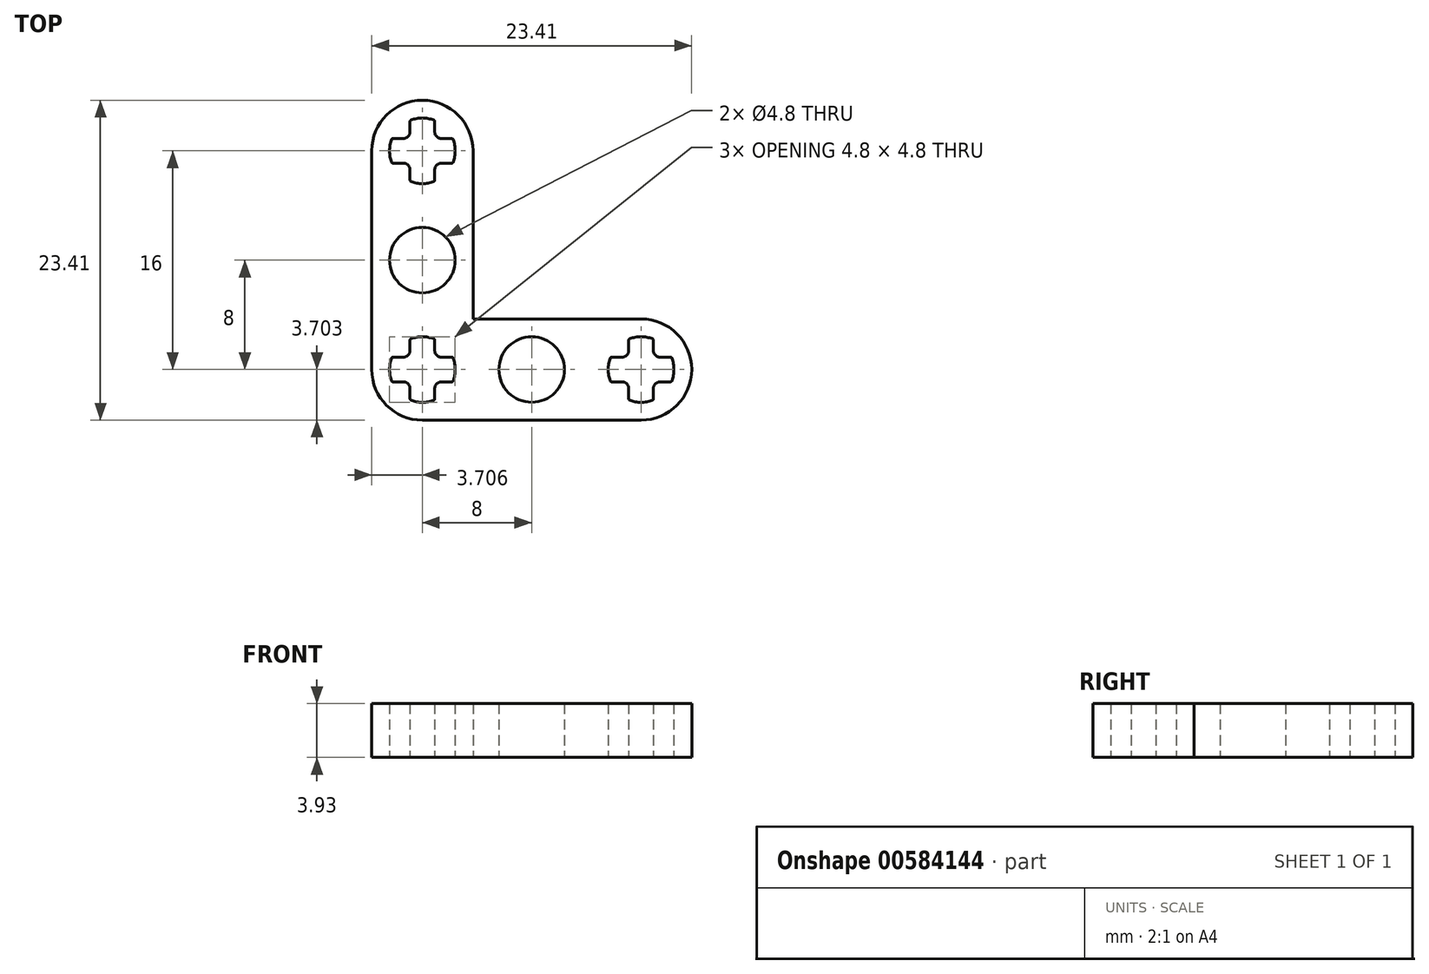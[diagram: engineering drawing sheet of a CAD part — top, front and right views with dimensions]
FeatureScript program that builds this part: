
annotation { "Feature Type Name" : "Feature", "Feature Type Description" : "" }
export const myFeature = defineFeature(function(context is Context, id is Id, definition is map)
    precondition{}
    {
        {
            var Q0;
            Q0=qCreatedBy(makeId("Top.planeOp"),FACE);
            var sketch = newSketch(context, id + "F0", { "sketchPlane" : qUnion([Q0])});
            skLineSegment(sketch, "E0.bottom", {"start": v(-14.73, 7.85) * mm, "end": v(-7.32, 7.85) * mm, "construction": true});
            skLineSegment(sketch, "E0.top", {"start": v(-14.73, -15.56) * mm, "end": v(8.68, -15.56) * mm, "construction": true});
            skLineSegment(sketch, "E0.left", {"start": v(-14.73, 7.85) * mm, "end": v(-14.73, -15.56) * mm, "construction": true});
            skLineSegment(sketch, "E0.right", {"start": v(8.68, 7.85) * mm, "end": v(8.68, -15.56) * mm, "construction": true});
            skLineSegment(sketch, "E1", {"start": v(-7.32, 7.85) * mm, "end": v(-7.32, -15.56) * mm, "construction": true});
            skLineSegment(sketch, "E2", {"start": v(-7.32, 7.85) * mm, "end": v(8.68, 7.85) * mm, "construction": true});
            skPoint(sketch, "E3.centerSnap0", {"position": v(-11.02, 7.85) * mm});
            skArc(sketch, "E4", {"start": v(-7.32, 4.14) * mm, "mid": v(-11.02, 7.85) * mm, "end": v(-14.73, 4.14) * mm});
            skLineSegment(sketch, "E5", {"start": v(-11.02, 9.43) * mm, "end": v(-11.02, 5.44) * mm, "construction": true});
            skLineSegment(sketch, "E6", {"start": v(-14.73, -15.56) * mm, "end": v(0.14, -0.69) * mm, "construction": true});
            skLineSegment(sketch, "E7", {"start": v(14.6, -3.86) * mm, "end": v(-27.46, -3.86) * mm, "construction": true});
            skPoint(sketch, "E7.startSnap0", {"position": v(8.68, -3.86) * mm});
            skCircle(sketch, "E8", {"center": v(-11.02, -3.86) * mm, "radius": 2.4 * mm});
            skLineSegment(sketch, "E9", {"start": v(-7.32, 4.14) * mm, "end": v(-7.32, -8.15) * mm});
            skLineSegment(sketch, "E10", {"start": v(-14.73, 4.14) * mm, "end": v(-14.73, -15.56) * mm});
            skLineSegment(sketch, "E11.MirrorCS", {"start": v(8.68, -8.15) * mm, "end": v(-14.73, -8.15) * mm, "construction": true});
            skArc(sketch, "E12.MirrorCS", {"start": v(4.98, -8.15) * mm, "mid": v(8.68, -11.86) * mm, "end": v(4.98, -15.56) * mm});
            skLineSegment(sketch, "E13.MirrorCS", {"start": v(4.98, -15.56) * mm, "end": v(-14.73, -15.56) * mm});
            skLineSegment(sketch, "E14.MirrorCS", {"start": v(4.98, -8.15) * mm, "end": v(-7.32, -8.15) * mm});
            skCircle(sketch, "E15.MirrorC", {"center": v(-3.02, -11.86) * mm, "radius": 2.4 * mm});
            skLineSegment(sketch, "E16.0", {"start": v(-11.92, 5.54) * mm, "end": v(-11.92, 6.3) * mm});
            skArc(sketch, "E16.1", {"start": v(-11.92, 6.3) * mm, "mid": v(-11.9, 6.36) * mm, "end": v(-11.86, 6.4) * mm});
            skArc(sketch, "E16.2", {"start": v(-11.86, 6.4) * mm, "mid": v(-11.02, 6.54) * mm, "end": v(-10.19, 6.4) * mm});
            skArc(sketch, "E16.3", {"start": v(-10.19, 6.4) * mm, "mid": v(-10.14, 6.36) * mm, "end": v(-10.12, 6.3) * mm});
            skLineSegment(sketch, "E16.4", {"start": v(-10.12, 6.3) * mm, "end": v(-10.12, 5.54) * mm});
            skArc(sketch, "E16.5", {"start": v(-10.12, 5.54) * mm, "mid": v(-9.98, 5.19) * mm, "end": v(-9.62, 5.04) * mm});
            skLineSegment(sketch, "E16.6", {"start": v(-9.62, 5.04) * mm, "end": v(-8.87, 5.04) * mm});
            skArc(sketch, "E16.7", {"start": v(-12.42, 5.04) * mm, "mid": v(-12.07, 5.19) * mm, "end": v(-11.92, 5.54) * mm});
            skLineSegment(sketch, "E16.8", {"start": v(-13.18, 5.04) * mm, "end": v(-12.42, 5.04) * mm});
            skArc(sketch, "E16.10", {"start": v(-13.27, 4.98) * mm, "mid": v(-13.24, 5.02) * mm, "end": v(-13.18, 5.04) * mm});
            skArc(sketch, "E16.11", {"start": v(-8.87, 5.04) * mm, "mid": v(-8.81, 5.02) * mm, "end": v(-8.77, 4.98) * mm});
            skArc(sketch, "E16.12", {"start": v(-8.77, 4.98) * mm, "mid": v(-8.66, 4.57) * mm, "end": v(-8.62, 4.14) * mm});
            skPoint(sketch, "E17.startSnap0", {"position": v(-13.42, 4.14) * mm});
            skArc(sketch, "E18", {"start": v(-13.42, 4.14) * mm, "mid": v(-13.39, 4.57) * mm, "end": v(-13.27, 4.98) * mm});
            skLineSegment(sketch, "E19", {"start": v(-13.42, 4.14) * mm, "end": v(-8.62, 4.14) * mm, "construction": true});
            skLineSegment(sketch, "E20", {"start": v(-13.42, 4.14) * mm, "end": v(-13.42, 1.48) * mm, "construction": true});
            skArc(sketch, "E21.MirrorCS", {"start": v(-13.42, 4.14) * mm, "mid": v(-13.39, 3.72) * mm, "end": v(-13.27, 3.3) * mm});
            skArc(sketch, "E22.MirrorCS", {"start": v(-13.27, 3.3) * mm, "mid": v(-13.24, 3.26) * mm, "end": v(-13.18, 3.24) * mm});
            skLineSegment(sketch, "E23.MirrorCS", {"start": v(-13.18, 3.24) * mm, "end": v(-12.42, 3.24) * mm});
            skArc(sketch, "E24.MirrorCS", {"start": v(-12.42, 3.24) * mm, "mid": v(-12.07, 3.1) * mm, "end": v(-11.92, 2.74) * mm});
            skLineSegment(sketch, "E25.MirrorCS", {"start": v(-11.92, 2.74) * mm, "end": v(-11.92, 1.99) * mm});
            skArc(sketch, "E26.MirrorCS", {"start": v(-11.92, 1.99) * mm, "mid": v(-11.9, 1.93) * mm, "end": v(-11.86, 1.9) * mm});
            skArc(sketch, "E27.MirrorCS", {"start": v(-11.86, 1.9) * mm, "mid": v(-11.02, 1.74) * mm, "end": v(-10.19, 1.9) * mm});
            skArc(sketch, "E28.MirrorCS", {"start": v(-10.19, 1.9) * mm, "mid": v(-10.14, 1.93) * mm, "end": v(-10.12, 1.99) * mm});
            skLineSegment(sketch, "E29.MirrorCS", {"start": v(-10.12, 1.99) * mm, "end": v(-10.12, 2.74) * mm});
            skArc(sketch, "E30.MirrorCS", {"start": v(-10.12, 2.74) * mm, "mid": v(-9.98, 3.1) * mm, "end": v(-9.62, 3.24) * mm});
            skLineSegment(sketch, "E31.MirrorCS", {"start": v(-9.62, 3.24) * mm, "end": v(-8.87, 3.24) * mm});
            skArc(sketch, "E32.MirrorCS", {"start": v(-8.87, 3.24) * mm, "mid": v(-8.81, 3.26) * mm, "end": v(-8.77, 3.3) * mm});
            skArc(sketch, "E33.MirrorCS", {"start": v(-8.77, 3.3) * mm, "mid": v(-8.66, 3.72) * mm, "end": v(-8.62, 4.14) * mm});
            skArc(sketch, "E34.MirrorCS", {"start": v(4.98, -14.26) * mm, "mid": v(5.4, -14.22) * mm, "end": v(5.81, -14.1) * mm});
            skArc(sketch, "E35.MirrorCS", {"start": v(5.81, -14.1) * mm, "mid": v(5.86, -14.07) * mm, "end": v(5.88, -14.01) * mm});
            skLineSegment(sketch, "E36.MirrorCS", {"start": v(5.88, -14.01) * mm, "end": v(5.88, -13.26) * mm});
            skArc(sketch, "E37.MirrorCS", {"start": v(5.88, -13.26) * mm, "mid": v(6.02, -12.9) * mm, "end": v(6.38, -12.76) * mm});
            skLineSegment(sketch, "E38.MirrorCS", {"start": v(6.38, -12.76) * mm, "end": v(7.13, -12.76) * mm});
            skArc(sketch, "E39.MirrorCS", {"start": v(7.13, -12.76) * mm, "mid": v(7.19, -12.74) * mm, "end": v(7.23, -12.7) * mm});
            skArc(sketch, "E40.MirrorCS", {"start": v(7.23, -12.7) * mm, "mid": v(7.38, -11.86) * mm, "end": v(7.23, -11.02) * mm});
            skArc(sketch, "E41.MirrorCS", {"start": v(7.23, -11.02) * mm, "mid": v(7.19, -10.98) * mm, "end": v(7.13, -10.96) * mm});
            skLineSegment(sketch, "E42.MirrorCS", {"start": v(7.13, -10.96) * mm, "end": v(6.38, -10.96) * mm});
            skArc(sketch, "E43.MirrorCS", {"start": v(6.38, -10.96) * mm, "mid": v(6.02, -10.81) * mm, "end": v(5.88, -10.46) * mm});
            skLineSegment(sketch, "E44.MirrorCS", {"start": v(5.88, -10.46) * mm, "end": v(5.88, -9.7) * mm});
            skArc(sketch, "E45.MirrorCS", {"start": v(5.88, -9.7) * mm, "mid": v(5.86, -9.64) * mm, "end": v(5.81, -9.6) * mm});
            skArc(sketch, "E46.MirrorCS", {"start": v(5.81, -9.6) * mm, "mid": v(5.4, -9.5) * mm, "end": v(4.98, -9.46) * mm});
            skArc(sketch, "E47.MirrorCS", {"start": v(4.14, -9.6) * mm, "mid": v(4.55, -9.5) * mm, "end": v(4.98, -9.46) * mm});
            skArc(sketch, "E48.MirrorCS", {"start": v(4.08, -9.7) * mm, "mid": v(4.1, -9.64) * mm, "end": v(4.14, -9.6) * mm});
            skLineSegment(sketch, "E49.MirrorCS", {"start": v(4.08, -10.46) * mm, "end": v(4.08, -9.7) * mm});
            skArc(sketch, "E50.MirrorCS", {"start": v(3.58, -10.96) * mm, "mid": v(3.93, -10.81) * mm, "end": v(4.08, -10.46) * mm});
            skLineSegment(sketch, "E51.MirrorCS", {"start": v(2.82, -10.96) * mm, "end": v(3.58, -10.96) * mm});
            skArc(sketch, "E52.MirrorCS", {"start": v(2.73, -11.02) * mm, "mid": v(2.76, -10.98) * mm, "end": v(2.82, -10.96) * mm});
            skArc(sketch, "E53.MirrorCS", {"start": v(2.73, -12.7) * mm, "mid": v(2.58, -11.86) * mm, "end": v(2.73, -11.02) * mm});
            skArc(sketch, "E54.MirrorCS", {"start": v(2.82, -12.76) * mm, "mid": v(2.76, -12.74) * mm, "end": v(2.73, -12.7) * mm});
            skLineSegment(sketch, "E55.MirrorCS", {"start": v(3.58, -12.76) * mm, "end": v(2.82, -12.76) * mm});
            skArc(sketch, "E56.MirrorCS", {"start": v(4.08, -13.26) * mm, "mid": v(3.93, -12.9) * mm, "end": v(3.58, -12.76) * mm});
            skLineSegment(sketch, "E57.MirrorCS", {"start": v(4.08, -14.01) * mm, "end": v(4.08, -13.26) * mm});
            skArc(sketch, "E58.MirrorCS", {"start": v(4.14, -14.1) * mm, "mid": v(4.1, -14.07) * mm, "end": v(4.08, -14.01) * mm});
            skArc(sketch, "E59.MirrorCS", {"start": v(4.98, -14.26) * mm, "mid": v(4.55, -14.22) * mm, "end": v(4.14, -14.1) * mm});
            skArc(sketch, "E60.0.1.0", {"start": v(-8.77, -12.7) * mm, "mid": v(-8.66, -12.28) * mm, "end": v(-8.62, -11.86) * mm});
            skArc(sketch, "E60.0.1.1", {"start": v(-13.42, -11.86) * mm, "mid": v(-13.39, -11.43) * mm, "end": v(-13.27, -11.02) * mm});
            skLineSegment(sketch, "E60.0.1.2", {"start": v(-13.42, -11.86) * mm, "end": v(-8.62, -11.86) * mm, "construction": true});
            skArc(sketch, "E60.0.1.3", {"start": v(-10.12, -10.46) * mm, "mid": v(-9.98, -10.81) * mm, "end": v(-9.62, -10.96) * mm});
            skArc(sketch, "E60.0.1.4", {"start": v(-13.42, -11.86) * mm, "mid": v(-13.39, -12.28) * mm, "end": v(-13.27, -12.7) * mm});
            skArc(sketch, "E60.0.1.5", {"start": v(-10.12, -13.26) * mm, "mid": v(-9.98, -12.9) * mm, "end": v(-9.62, -12.76) * mm});
            skLineSegment(sketch, "E60.0.1.6", {"start": v(-11.02, -6.57) * mm, "end": v(-11.02, -10.56) * mm, "construction": true});
            skLineSegment(sketch, "E60.0.1.7", {"start": v(-9.62, -10.96) * mm, "end": v(-8.87, -10.96) * mm});
            skArc(sketch, "E60.0.1.8", {"start": v(-11.86, -14.1) * mm, "mid": v(-11.02, -14.26) * mm, "end": v(-10.19, -14.1) * mm});
            skLineSegment(sketch, "E60.0.1.9", {"start": v(-10.12, -9.7) * mm, "end": v(-10.12, -10.46) * mm});
            skArc(sketch, "E60.0.1.10", {"start": v(-8.77, -11.02) * mm, "mid": v(-8.66, -11.43) * mm, "end": v(-8.62, -11.86) * mm});
            skPoint(sketch, "E60.0.1.11", {"position": v(-13.42, -11.86) * mm});
            skLineSegment(sketch, "E60.0.1.12", {"start": v(-9.62, -12.76) * mm, "end": v(-8.87, -12.76) * mm});
            skLineSegment(sketch, "E60.0.1.13", {"start": v(-13.18, -12.76) * mm, "end": v(-12.42, -12.76) * mm});
            skLineSegment(sketch, "E60.0.1.14", {"start": v(-10.12, -14.01) * mm, "end": v(-10.12, -13.26) * mm});
            skLineSegment(sketch, "E60.0.1.15", {"start": v(-13.18, -10.96) * mm, "end": v(-12.42, -10.96) * mm});
            skLineSegment(sketch, "E60.0.1.16", {"start": v(-13.42, -11.86) * mm, "end": v(-13.42, -14.52) * mm, "construction": true});
            skLineSegment(sketch, "E60.0.1.17", {"start": v(-11.92, -13.26) * mm, "end": v(-11.92, -14.01) * mm});
            skArc(sketch, "E60.0.1.18", {"start": v(-12.42, -10.96) * mm, "mid": v(-12.07, -10.81) * mm, "end": v(-11.92, -10.46) * mm});
            skArc(sketch, "E60.0.1.19", {"start": v(-12.42, -12.76) * mm, "mid": v(-12.07, -12.9) * mm, "end": v(-11.92, -13.26) * mm});
            skLineSegment(sketch, "E60.0.1.20", {"start": v(-11.92, -10.46) * mm, "end": v(-11.92, -9.7) * mm});
            skArc(sketch, "E60.0.1.21", {"start": v(-10.19, -14.1) * mm, "mid": v(-10.14, -14.07) * mm, "end": v(-10.12, -14.01) * mm});
            skArc(sketch, "E60.0.1.22", {"start": v(-8.87, -10.96) * mm, "mid": v(-8.81, -10.98) * mm, "end": v(-8.77, -11.02) * mm});
            skArc(sketch, "E60.0.1.23", {"start": v(-11.92, -14.01) * mm, "mid": v(-11.9, -14.07) * mm, "end": v(-11.86, -14.1) * mm});
            skArc(sketch, "E60.0.1.24", {"start": v(-8.87, -12.76) * mm, "mid": v(-8.81, -12.74) * mm, "end": v(-8.77, -12.7) * mm});
            skArc(sketch, "E60.0.1.25", {"start": v(-13.27, -11.02) * mm, "mid": v(-13.24, -10.98) * mm, "end": v(-13.18, -10.96) * mm});
            skArc(sketch, "E60.0.1.26", {"start": v(-13.27, -12.7) * mm, "mid": v(-13.24, -12.74) * mm, "end": v(-13.18, -12.76) * mm});
            skArc(sketch, "E60.0.1.27", {"start": v(-10.19, -9.6) * mm, "mid": v(-10.14, -9.64) * mm, "end": v(-10.12, -9.7) * mm});
            skArc(sketch, "E60.0.1.28", {"start": v(-11.86, -9.6) * mm, "mid": v(-11.02, -9.46) * mm, "end": v(-10.19, -9.6) * mm});
            skArc(sketch, "E60.0.1.29", {"start": v(-11.92, -9.7) * mm, "mid": v(-11.9, -9.64) * mm, "end": v(-11.86, -9.6) * mm});
            skLineSegment(sketch, "E60.0.1.30", {"start": v(-14.73, -8.15) * mm, "end": v(-14.73, -31.56) * mm, "construction": true});
            skLineSegment(sketch, "E60.direction1", {"start": v(-13.42, 1.48) * mm, "end": v(24.38, 1.48) * mm, "construction": true});
            skLineSegment(sketch, "E60.direction2", {"start": v(-13.42, 1.48) * mm, "end": v(-13.42, -14.52) * mm, "construction": true});
            skSolve(sketch);
        }
        {
            var Q0;
            Q0=makeQuery(id+"F0.imprint","IMPRINT",FACE,{"disambiguationData":[TD([[makeQuery(id+"F0.imprint","IMPRINT",EDGE,{"derivedFrom":sQuery(id+"F0.wireOp",EDGE,"E4")}),1.0]])]});
            extrude(context, id + "F1", {"entities" : qUnion([Q0]), "depth" : 3.93 * mm, "offsetDistance" : 25 * mm});
        }
        {
            var Q0;
            Q0=makeQuery(id+"F1.opExtrude","SWEPT_EDGE",EDGE,{"disambiguationData":[OSD([sQuery(id+"F0.wireOp",EDGE,"E10"),sQuery(id+"F0.wireOp",EDGE,"E13.MirrorCS")])]});
            fillet(context, id + "F2", {"entities" : qUnion([Q0]), "radius" : (7.4 / 2) * mm, "tangentPropagation" : true, "allowEdgeOverflow" : false});
        }
    });
